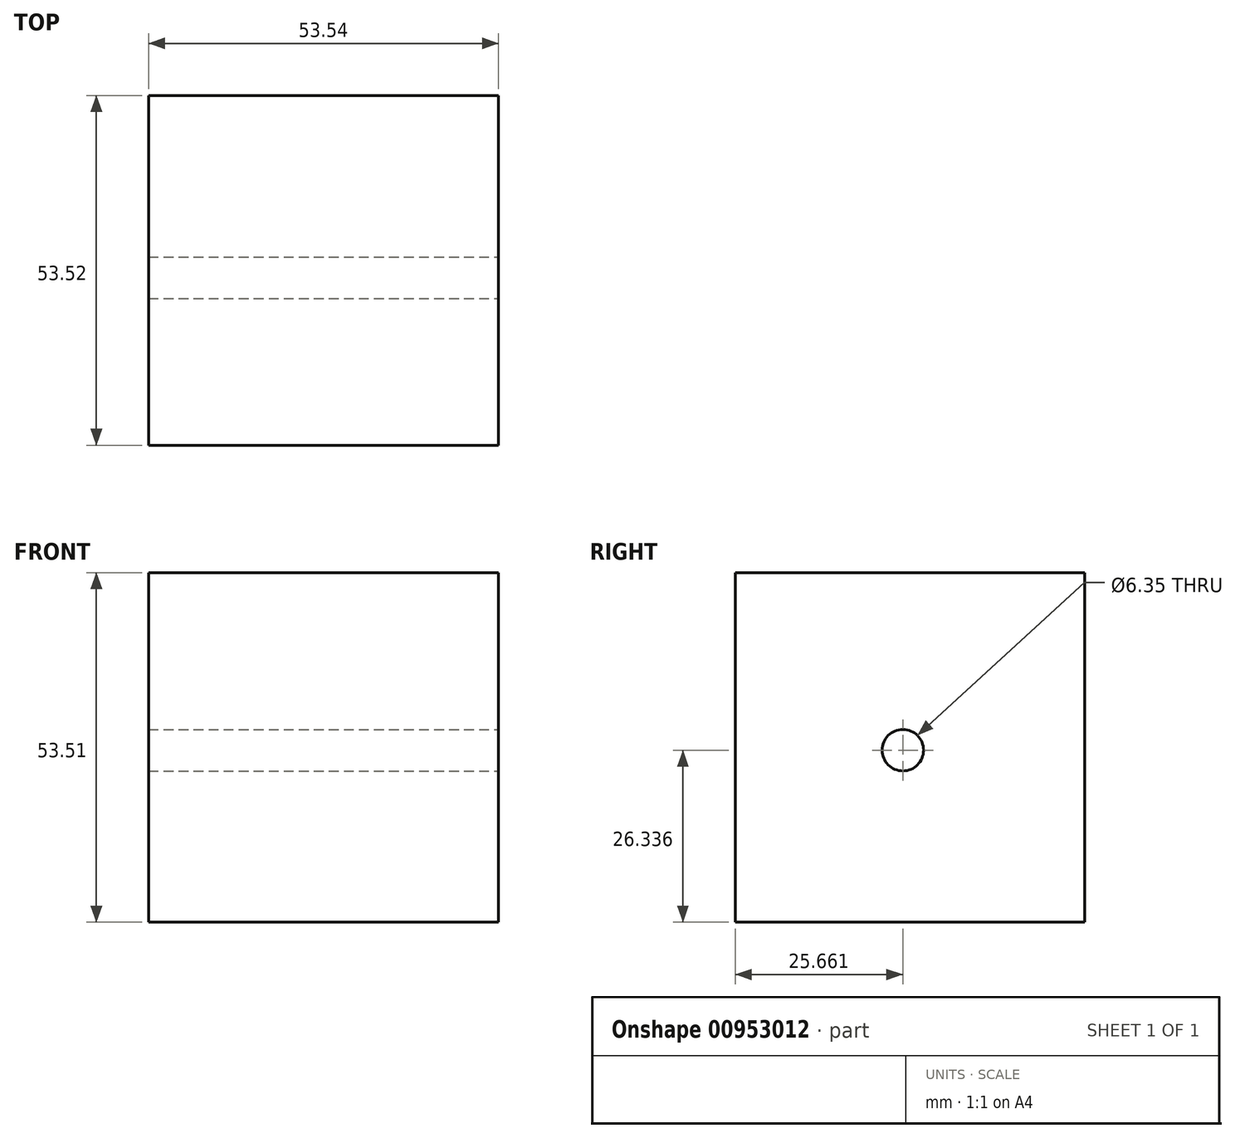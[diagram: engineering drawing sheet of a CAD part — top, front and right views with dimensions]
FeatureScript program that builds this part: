
annotation { "Feature Type Name" : "Feature", "Feature Type Description" : "" }
export const myFeature = defineFeature(function(context is Context, id is Id, definition is map)
    precondition{}
    {
        {
            var Q0;
            Q0=qCreatedBy(makeId("Front.planeOp"),FACE);
            var sketch = newSketch(context, id + "F0", { "sketchPlane" : qUnion([Q0])});
            skLineSegment(sketch, "E0", {"start": v(-61.5, 53.5) * mm, "end": v(-61.5, 0) * mm});
            skLineSegment(sketch, "E1", {"start": v(-61.5, 0) * mm, "end": v(-7.97, 0) * mm});
            skLineSegment(sketch, "E2", {"start": v(-7.97, 0) * mm, "end": v(-7.97, 53.5) * mm});
            skLineSegment(sketch, "E3", {"start": v(-61.5, 53.5) * mm, "end": v(-7.97, 53.5) * mm});
            skSolve(sketch);
        }
        {
            var Q0;
            Q0=makeQuery(id+"F0.imprint","IMPRINT",FACE,{"disambiguationData":[TD([[makeQuery(id+"F0.imprint","IMPRINT",EDGE,{"derivedFrom":sQuery(id+"F0.wireOp",EDGE,"E0")}),1.0]])]});
            var Q1;
            Q1=sQuery(id+"F0.wireOp",EDGE,"E3");
            extrude(context, id + "F1", {"entities" : qUnion([Q0]), "surfaceEntities" : qUnion([Q1]), "depth" : 53.52 * mm, "offsetDistance" : 25.4 * mm});
        }
        {
            var Q0;
            Q0=qCreatedBy(makeId("Right.planeOp"),FACE);
            var sketch = newSketch(context, id + "F2", { "sketchPlane" : qUnion([Q0])});
            skCircle(sketch, "E4", {"center": v(-27.86, 26.34) * mm, "radius": 3.18 * mm});
            skSolve(sketch);
        }
        {
            var Q0;
            Q0=sQuery(id+"F2.wireOp",VERTEX,"E4.center");
            var Q1;
            Q1=makeQuery(id+"F1.opExtrude","SWEPT_BODY",BODY,{"disambiguationData":[OSD([sQuery(id+"F0.wireOp",EDGE,"E0"),sQuery(id+"F0.wireOp",EDGE,"E1"),sQuery(id+"F0.wireOp",EDGE,"E2"),sQuery(id+"F0.wireOp",EDGE,"E3")])]});
            hole(context, id + "F3", {"style" : HoleStyle.SIMPLE, "endStyle" : HoleEndStyle.THROUGH, "holeDiameter" : 6.35 * mm, "majorDiameter" : 6.35 * mm, "isTappedThrough" : true, "tappedDepth" : 12.7 * mm, "tapClearance" : 3, "locations" : qUnion([Q0]), "scope" : qUnion([Q1])});
        }
    });
